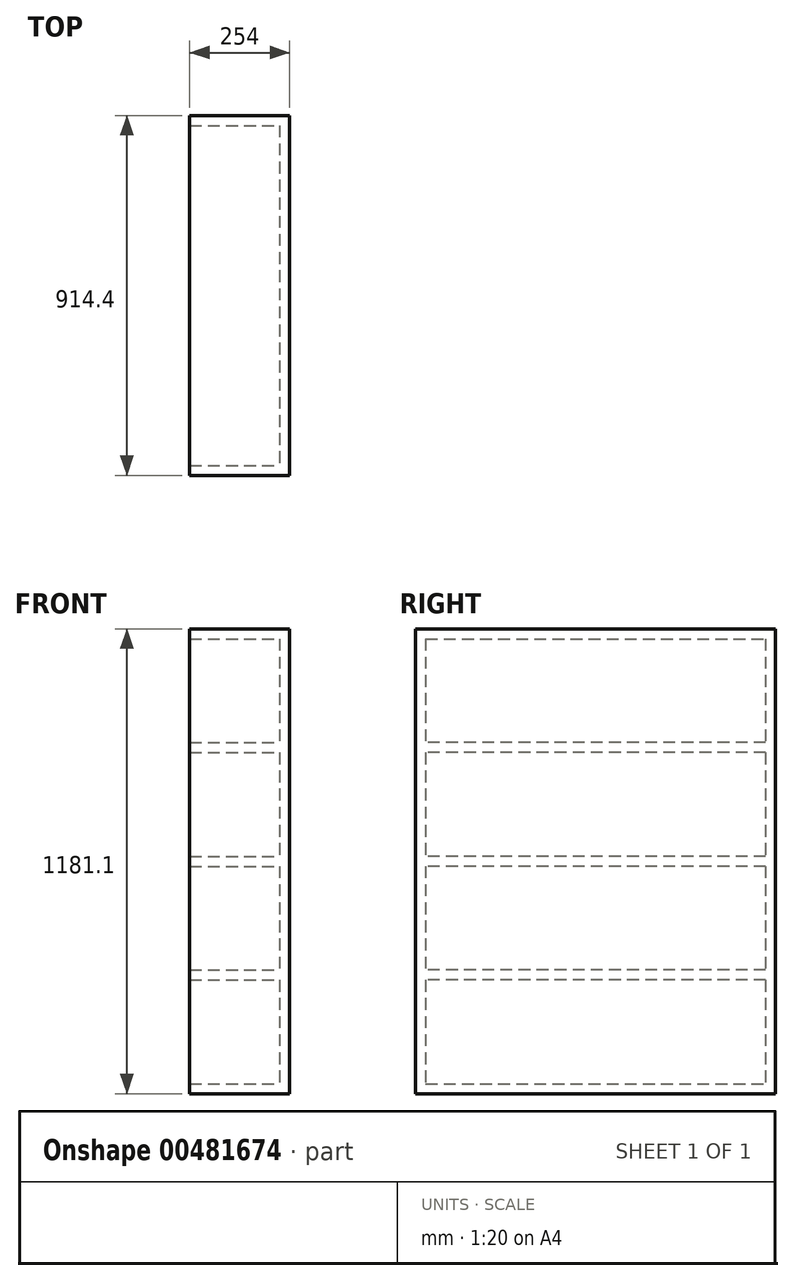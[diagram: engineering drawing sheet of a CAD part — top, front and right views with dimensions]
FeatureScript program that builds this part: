
annotation { "Feature Type Name" : "Feature", "Feature Type Description" : "" }
export const myFeature = defineFeature(function(context is Context, id is Id, definition is map)
    precondition{}
    {
        {
            var Q0;
            Q0=qCreatedBy(makeId("Right.planeOp"),FACE);
            var sketch = newSketch(context, id + "F0", { "sketchPlane" : qUnion([Q0])});
            skLineSegment(sketch, "E0.bottom", {"start": v(-457.2, 590.55) * mm, "end": v(457.2, 590.55) * mm});
            skLineSegment(sketch, "E0.top", {"start": v(-457.2, -590.55) * mm, "end": v(457.2, -590.55) * mm});
            skLineSegment(sketch, "E0.left", {"start": v(-457.2, 590.55) * mm, "end": v(-457.2, -590.55) * mm});
            skLineSegment(sketch, "E0.right", {"start": v(457.2, 590.55) * mm, "end": v(457.2, -590.55) * mm});
            skPoint(sketch, "E0.middle", {"position": v(0, 0) * mm});
            skSolve(sketch);
        }
        {
            var Q0;
            Q0=makeQuery(id+"F0.imprint","IMPRINT",FACE,{"disambiguationData":[TD([[makeQuery(id+"F0.imprint","IMPRINT",EDGE,{"derivedFrom":sQuery(id+"F0.wireOp",EDGE,"E0.bottom")}),-1.0]])]});
            extrude(context, id + "F1", {"entities" : qUnion([Q0]), "depth" : 25.4 * mm});
        }
        {
            var Q0;
            Q0=makeQuery(id+"F1.opExtrude","CAP_FACE",FACE,{"disambiguationData":[OSD([sQuery(id+"F0.wireOp",EDGE,"E0.bottom"),sQuery(id+"F0.wireOp",EDGE,"E0.top"),sQuery(id+"F0.wireOp",EDGE,"E0.left"),sQuery(id+"F0.wireOp",EDGE,"E0.right")])],"isStart":true});
            var sketch = newSketch(context, id + "F2", { "sketchPlane" : qUnion([Q0])});
            skLineSegment(sketch, "E1.0", {"start": v(457.2, 590.55) * mm, "end": v(-457.2, 590.55) * mm});
            skLineSegment(sketch, "E2.0", {"start": v(-457.2, 590.55) * mm, "end": v(-457.2, -590.55) * mm});
            skLineSegment(sketch, "E3.0", {"start": v(457.2, -590.55) * mm, "end": v(-457.2, -590.55) * mm});
            skLineSegment(sketch, "E4.0", {"start": v(457.2, 590.55) * mm, "end": v(457.2, -590.55) * mm});
            skLineSegment(sketch, "E5.0", {"start": v(431.8, 565.15) * mm, "end": v(-431.8, 565.15) * mm});
            skLineSegment(sketch, "E5.1", {"start": v(431.8, 565.15) * mm, "end": v(431.8, -565.15) * mm});
            skLineSegment(sketch, "E5.2", {"start": v(431.8, -565.15) * mm, "end": v(-431.8, -565.15) * mm});
            skLineSegment(sketch, "E5.3", {"start": v(-431.8, 565.15) * mm, "end": v(-431.8, -565.15) * mm});
            skLineSegment(sketch, "E6.bottom", {"start": v(-431.8, 301.63) * mm, "end": v(431.8, 301.63) * mm});
            skLineSegment(sketch, "E6.top", {"start": v(-431.8, 276.23) * mm, "end": v(431.8, 276.23) * mm});
            skLineSegment(sketch, "E6.left", {"start": v(-431.8, 301.63) * mm, "end": v(-431.8, 276.23) * mm});
            skLineSegment(sketch, "E6.right", {"start": v(431.8, 301.63) * mm, "end": v(431.8, 276.23) * mm});
            skLineSegment(sketch, "E7.bottom", {"start": v(-431.8, 12.7) * mm, "end": v(431.8, 12.7) * mm});
            skLineSegment(sketch, "E7.top", {"start": v(-431.8, -12.7) * mm, "end": v(431.8, -12.7) * mm});
            skLineSegment(sketch, "E7.left", {"start": v(-431.8, 12.7) * mm, "end": v(-431.8, -12.7) * mm});
            skLineSegment(sketch, "E7.right", {"start": v(431.8, 12.7) * mm, "end": v(431.8, -12.7) * mm});
            skLineSegment(sketch, "E8.bottom", {"start": v(-431.8, -276.23) * mm, "end": v(431.8, -276.22) * mm});
            skLineSegment(sketch, "E8.top", {"start": v(-431.8, -301.63) * mm, "end": v(431.8, -301.62) * mm});
            skLineSegment(sketch, "E8.left", {"start": v(-431.8, -276.23) * mm, "end": v(-431.8, -301.63) * mm});
            skLineSegment(sketch, "E8.right", {"start": v(431.8, -276.22) * mm, "end": v(431.8, -301.62) * mm});
            skLineSegment(sketch, "E9", {"start": v(0, 565.15) * mm, "end": v(0, 301.63) * mm, "construction": true});
            skLineSegment(sketch, "E10", {"start": v(0, 301.63) * mm, "end": v(0, 276.23) * mm, "construction": true});
            skLineSegment(sketch, "E11", {"start": v(0, 276.23) * mm, "end": v(0, 12.7) * mm, "construction": true});
            skLineSegment(sketch, "E12", {"start": v(0, -12.7) * mm, "end": v(0, -276.22) * mm, "construction": true});
            skLineSegment(sketch, "E13", {"start": v(0, -301.62) * mm, "end": v(0, -565.15) * mm, "construction": true});
            skSolve(sketch);
        }
        {
            var Q0;
            Q0=makeQuery(id+"F2.imprint","IMPRINT",FACE,{"disambiguationData":[TD([[makeQuery(id+"F2.imprint","IMPRINT",EDGE,{"derivedFrom":sQuery(id+"F2.wireOp",EDGE,"E1.0")}),1.0]])]});
            var Q1;
            Q1=makeQuery(id+"F2.imprint","IMPRINT",FACE,{"disambiguationData":[TD([[makeQuery(id+"F2.imprint","IMPRINT",EDGE,{"derivedFrom":sQuery(id+"F2.wireOp",EDGE,"E6.bottom")}),-1.0]])]});
            var Q2;
            Q2=makeQuery(id+"F2.imprint","IMPRINT",FACE,{"disambiguationData":[TD([[makeQuery(id+"F2.imprint","IMPRINT",EDGE,{"derivedFrom":sQuery(id+"F2.wireOp",EDGE,"E7.bottom")}),-1.0]])]});
            var Q3;
            Q3=makeQuery(id+"F2.imprint","IMPRINT",FACE,{"disambiguationData":[TD([[makeQuery(id+"F2.imprint","IMPRINT",EDGE,{"derivedFrom":sQuery(id+"F2.wireOp",EDGE,"E8.bottom")}),-1.0]])]});
            extrude(context, id + "F3", {"entities" : qUnion([Q0, Q1, Q2, Q3]), "operationType" : NewBodyOperationType.ADD, "depth" : 228.6 * mm});
        }
    });
